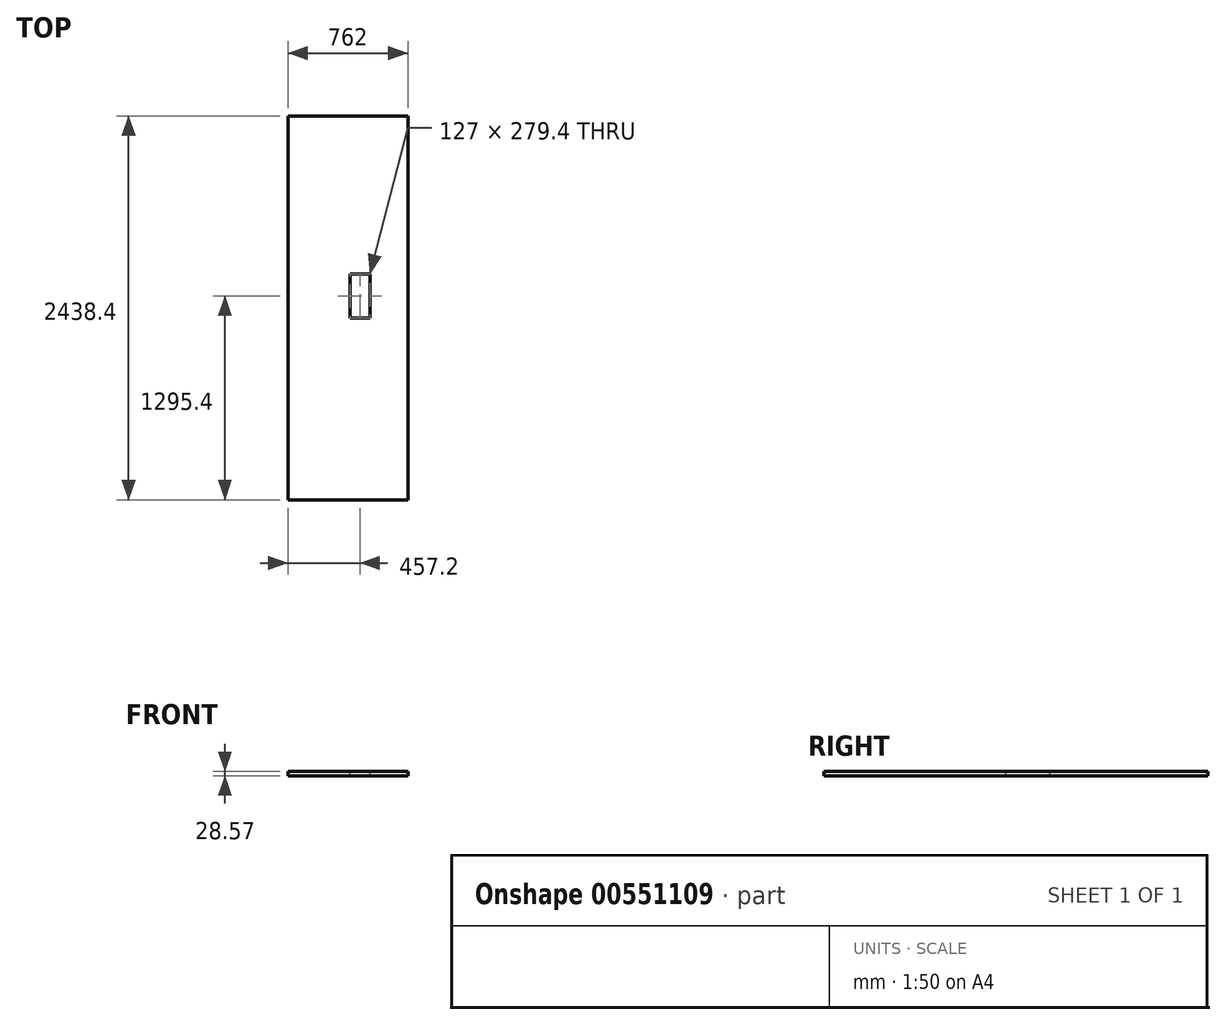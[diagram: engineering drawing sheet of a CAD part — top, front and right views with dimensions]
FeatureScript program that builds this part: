
annotation { "Feature Type Name" : "Feature", "Feature Type Description" : "" }
export const myFeature = defineFeature(function(context is Context, id is Id, definition is map)
    precondition{}
    {
        {
            var Q0;
            Q0=qCreatedBy(makeId("Top.planeOp"),FACE);
            var sketch = newSketch(context, id + "F0", { "sketchPlane" : qUnion([Q0])});
            skLineSegment(sketch, "E0.bottom", {"start": v(381, 1066.8) * mm, "end": v(-381, 1066.8) * mm});
            skLineSegment(sketch, "E0.top", {"start": v(381, -1066.8) * mm, "end": v(-381, -1066.8) * mm});
            skLineSegment(sketch, "E0.left", {"start": v(381, 1066.8) * mm, "end": v(381, -1066.8) * mm});
            skLineSegment(sketch, "E0.right", {"start": v(-381, 1066.8) * mm, "end": v(-381, -1066.8) * mm});
            skPoint(sketch, "E0.middle", {"position": v(0, 0) * mm});
            skSolve(sketch);
        }
        {
            var Q0;
            Q0=makeQuery(id+"F0.imprint","IMPRINT",FACE,{"disambiguationData":[TD([[makeQuery(id+"F0.imprint","IMPRINT",EDGE,{"derivedFrom":sQuery(id+"F0.wireOp",EDGE,"E0.bottom")}),1.0]])]});
            extrude(context, id + "F1", {"entities" : qUnion([Q0]), "depth" : 28.57 * mm, "offsetDistance" : 25.4 * mm});
        }
        {
            var Q0;
            Q0=makeQuery(id+"F1.opExtrude","CAP_FACE",FACE,{"disambiguationData":[OSD([sQuery(id+"F0.wireOp",EDGE,"E0.bottom"),sQuery(id+"F0.wireOp",EDGE,"E0.top"),sQuery(id+"F0.wireOp",EDGE,"E0.left"),sQuery(id+"F0.wireOp",EDGE,"E0.right")])],"isStart":false});
            var sketch = newSketch(context, id + "F2", { "sketchPlane" : qUnion([Q0])});
            skLineSegment(sketch, "E1", {"start": v(0, 1066.8) * mm, "end": v(0, -76.2) * mm});
            skLineSegment(sketch, "E2", {"start": v(0, -76.2) * mm, "end": v(76.2, -76.2) * mm});
            skLineSegment(sketch, "E3.bottom", {"start": v(12.7, -215.9) * mm, "end": v(139.7, -215.9) * mm});
            skLineSegment(sketch, "E3.top", {"start": v(12.7, 63.5) * mm, "end": v(139.7, 63.5) * mm});
            skLineSegment(sketch, "E3.left", {"start": v(12.7, -215.9) * mm, "end": v(12.7, 63.5) * mm});
            skLineSegment(sketch, "E3.right", {"start": v(139.7, -215.9) * mm, "end": v(139.7, 63.5) * mm});
            skPoint(sketch, "E3.middle", {"position": v(76.2, -76.2) * mm});
            skSolve(sketch);
        }
        {
            var Q0;
            {var subQ3=sQuery(id+"F2.wireOp",EDGE,"E3.bottom");Q0=makeQuery(id+"F2.imprint","IMPRINT",FACE,{"disambiguationData":[TD([[makeQuery(id+"F2.imprint","IMPRINT",EDGE,{"derivedFrom":subQ3}),1.0]])]});}
            extrude(context, id + "F3", {"entities" : qUnion([Q0]), "operationType" : NewBodyOperationType.REMOVE, "oppositeDirection" : true, "depth" : 31.75 * mm, "offsetDistance" : 25.4 * mm});
        }
        {
            var Q0;
            Q0=makeQuery(id+"F1.opExtrude","SWEPT_FACE",FACE,{"disambiguationData":[OSD([sQuery(id+"F0.wireOp",EDGE,"E0.top")])]});
            extrude(context, id + "F4", {"entities" : qUnion([Q0]), "operationType" : NewBodyOperationType.ADD, "depth" : 304.8 * mm, "offsetDistance" : 25.4 * mm});
        }
    });
